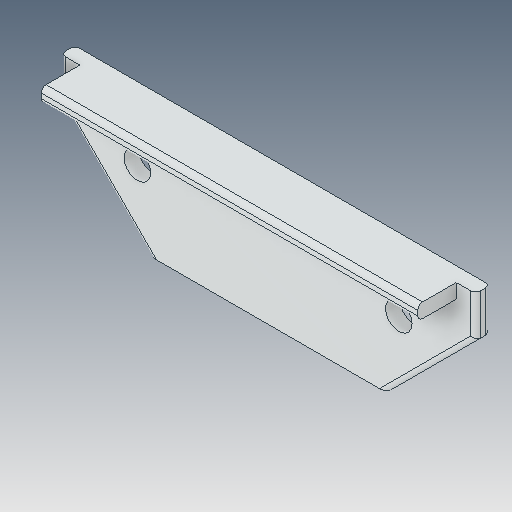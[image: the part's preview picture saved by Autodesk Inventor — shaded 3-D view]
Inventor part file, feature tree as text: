
AUTODESK INVENTOR PART (.ipt)
format: ipt  version: 2023.5 (Build 275446000, 446)  size: 109,056 bytes
history: native  units: in
note: dims shown in document units (in); Inventor stores cm internally (conversion verified against a paired STEP export)
features: fillet x1
ambient origin geometry x8: Origin, YZ Plane, XZ Plane, XY Plane, X Axis, Y Axis, Z Axis, Center Point
bodies: Solid1 (feature_tree)
feature tree (1):
  fillet  "Fillet1"  [1 undecoded]
note: 1 required parameter value undecoded (feature->parameter linkage not recoverable at this tier; creation-order binding heuristic only, values carry confidence <= 0.55)
